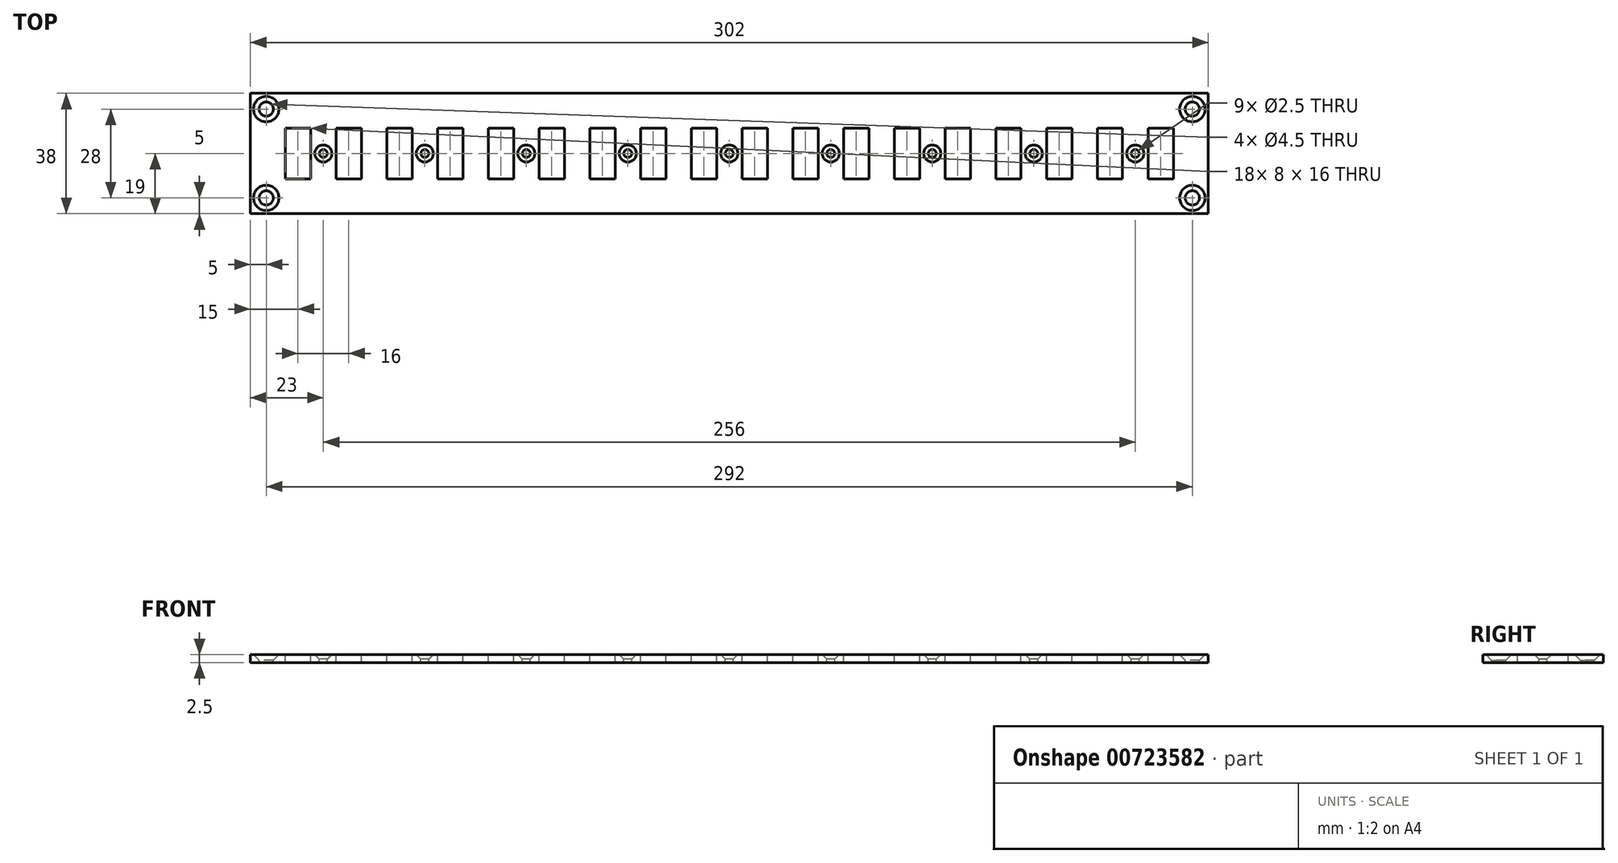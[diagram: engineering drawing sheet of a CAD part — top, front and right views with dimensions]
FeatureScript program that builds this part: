
annotation { "Feature Type Name" : "Feature", "Feature Type Description" : "" }
export const myFeature = defineFeature(function(context is Context, id is Id, definition is map)
    precondition{}
    {
        {
            var Q0;
            Q0=qCreatedBy(makeId("Top.planeOp"),FACE);
            var sketch = newSketch(context, id + "F0", { "sketchPlane" : qUnion([Q0])});
            skLineSegment(sketch, "E0.bottom", {"start": v(151, 19) * mm, "end": v(-151, 19) * mm});
            skLineSegment(sketch, "E0.top", {"start": v(151, -19) * mm, "end": v(-151, -19) * mm});
            skLineSegment(sketch, "E0.left", {"start": v(151, 19) * mm, "end": v(151, -19) * mm});
            skLineSegment(sketch, "E0.right", {"start": v(-151, 19) * mm, "end": v(-151, -19) * mm});
            skPoint(sketch, "E0.middle", {"position": v(0, 0) * mm});
            skLineSegment(sketch, "E1", {"start": v(-151, 0) * mm, "end": v(151, 0) * mm, "construction": true});
            skPoint(sketch, "E2", {"position": v(128, 0) * mm});
            skPoint(sketch, "E3", {"position": v(96, 0) * mm});
            skPoint(sketch, "E4", {"position": v(64, 0) * mm});
            skPoint(sketch, "E5", {"position": v(32, 0) * mm});
            skLineSegment(sketch, "E6", {"start": v(0, -19) * mm, "end": v(0, 19) * mm, "construction": true});
            skPoint(sketch, "E7.MirrorP", {"position": v(-32, 0) * mm});
            skPoint(sketch, "E8.MirrorP", {"position": v(-64, 0) * mm});
            skPoint(sketch, "E9.MirrorP", {"position": v(-96, 0) * mm});
            skPoint(sketch, "E10.MirrorP", {"position": v(-128, 0) * mm});
            skPoint(sketch, "E11", {"position": v(146, -14) * mm});
            skPoint(sketch, "E12.MirrorP", {"position": v(-146, -14) * mm});
            skPoint(sketch, "E13.MirrorP", {"position": v(146, 14) * mm});
            skPoint(sketch, "E14.MirrorP", {"position": v(-146, 14) * mm});
            skLineSegment(sketch, "E15", {"start": v(-151, 37.85) * mm, "end": v(-136, 37.85) * mm, "construction": true});
            skLineSegment(sketch, "E16", {"start": v(-136, 37.85) * mm, "end": v(-136, -40.42) * mm, "construction": true});
            skLineSegment(sketch, "E17.bottom", {"start": v(-132, 8) * mm, "end": v(-140, 8) * mm});
            skLineSegment(sketch, "E17.top", {"start": v(-132, -8) * mm, "end": v(-140, -8) * mm});
            skLineSegment(sketch, "E17.left", {"start": v(-132, 8) * mm, "end": v(-132, -8) * mm});
            skLineSegment(sketch, "E17.right", {"start": v(-140, 8) * mm, "end": v(-140, -8) * mm});
            skPoint(sketch, "E17.middle", {"position": v(-136, 0) * mm});
            skLineSegment(sketch, "E18.1.0.0", {"start": v(-116, 8) * mm, "end": v(-124, 8) * mm});
            skLineSegment(sketch, "E18.1.0.1", {"start": v(-116, 8) * mm, "end": v(-116, -8) * mm});
            skLineSegment(sketch, "E18.1.0.2", {"start": v(-124, 8) * mm, "end": v(-124, -8) * mm});
            skLineSegment(sketch, "E18.1.0.3", {"start": v(-116, -8) * mm, "end": v(-124, -8) * mm});
            skLineSegment(sketch, "E18.2.0.0", {"start": v(-100, 8) * mm, "end": v(-108, 8) * mm});
            skLineSegment(sketch, "E18.2.0.1", {"start": v(-100, 8) * mm, "end": v(-100, -8) * mm});
            skLineSegment(sketch, "E18.2.0.2", {"start": v(-108, 8) * mm, "end": v(-108, -8) * mm});
            skLineSegment(sketch, "E18.2.0.3", {"start": v(-100, -8) * mm, "end": v(-108, -8) * mm});
            skLineSegment(sketch, "E18.3.0.0", {"start": v(-84, 8) * mm, "end": v(-92, 8) * mm});
            skLineSegment(sketch, "E18.3.0.1", {"start": v(-84, 8) * mm, "end": v(-84, -8) * mm});
            skLineSegment(sketch, "E18.3.0.2", {"start": v(-92, 8) * mm, "end": v(-92, -8) * mm});
            skLineSegment(sketch, "E18.3.0.3", {"start": v(-84, -8) * mm, "end": v(-92, -8) * mm});
            skLineSegment(sketch, "E18.4.0.0", {"start": v(-68, 8) * mm, "end": v(-76, 8) * mm});
            skLineSegment(sketch, "E18.4.0.1", {"start": v(-68, 8) * mm, "end": v(-68, -8) * mm});
            skLineSegment(sketch, "E18.4.0.2", {"start": v(-76, 8) * mm, "end": v(-76, -8) * mm});
            skLineSegment(sketch, "E18.4.0.3", {"start": v(-68, -8) * mm, "end": v(-76, -8) * mm});
            skLineSegment(sketch, "E18.5.0.0", {"start": v(-52, 8) * mm, "end": v(-60, 8) * mm});
            skLineSegment(sketch, "E18.5.0.1", {"start": v(-52, 8) * mm, "end": v(-52, -8) * mm});
            skLineSegment(sketch, "E18.5.0.2", {"start": v(-60, 8) * mm, "end": v(-60, -8) * mm});
            skLineSegment(sketch, "E18.5.0.3", {"start": v(-52, -8) * mm, "end": v(-60, -8) * mm});
            skLineSegment(sketch, "E18.6.0.0", {"start": v(-36, 8) * mm, "end": v(-44, 8) * mm});
            skLineSegment(sketch, "E18.6.0.1", {"start": v(-36, 8) * mm, "end": v(-36, -8) * mm});
            skLineSegment(sketch, "E18.6.0.2", {"start": v(-44, 8) * mm, "end": v(-44, -8) * mm});
            skLineSegment(sketch, "E18.6.0.3", {"start": v(-36, -8) * mm, "end": v(-44, -8) * mm});
            skLineSegment(sketch, "E18.7.0.0", {"start": v(-20, 8) * mm, "end": v(-28, 8) * mm});
            skLineSegment(sketch, "E18.7.0.1", {"start": v(-20, 8) * mm, "end": v(-20, -8) * mm});
            skLineSegment(sketch, "E18.7.0.2", {"start": v(-28, 8) * mm, "end": v(-28, -8) * mm});
            skLineSegment(sketch, "E18.7.0.3", {"start": v(-20, -8) * mm, "end": v(-28, -8) * mm});
            skLineSegment(sketch, "E18.8.0.0", {"start": v(-4, 8) * mm, "end": v(-12, 8) * mm});
            skLineSegment(sketch, "E18.8.0.1", {"start": v(-4, 8) * mm, "end": v(-4, -8) * mm});
            skLineSegment(sketch, "E18.8.0.2", {"start": v(-12, 8) * mm, "end": v(-12, -8) * mm});
            skLineSegment(sketch, "E18.8.0.3", {"start": v(-4, -8) * mm, "end": v(-12, -8) * mm});
            skLineSegment(sketch, "E18.9.0.0", {"start": v(12, 8) * mm, "end": v(4, 8) * mm});
            skLineSegment(sketch, "E18.9.0.1", {"start": v(12, 8) * mm, "end": v(12, -8) * mm});
            skLineSegment(sketch, "E18.9.0.2", {"start": v(4, 8) * mm, "end": v(4, -8) * mm});
            skLineSegment(sketch, "E18.9.0.3", {"start": v(12, -8) * mm, "end": v(4, -8) * mm});
            skLineSegment(sketch, "E18.10.0.0", {"start": v(28, 8) * mm, "end": v(20, 8) * mm});
            skLineSegment(sketch, "E18.10.0.1", {"start": v(28, 8) * mm, "end": v(28, -8) * mm});
            skLineSegment(sketch, "E18.10.0.2", {"start": v(20, 8) * mm, "end": v(20, -8) * mm});
            skLineSegment(sketch, "E18.10.0.3", {"start": v(28, -8) * mm, "end": v(20, -8) * mm});
            skLineSegment(sketch, "E18.11.0.0", {"start": v(44, 8) * mm, "end": v(36, 8) * mm});
            skLineSegment(sketch, "E18.11.0.1", {"start": v(44, 8) * mm, "end": v(44, -8) * mm});
            skLineSegment(sketch, "E18.11.0.2", {"start": v(36, 8) * mm, "end": v(36, -8) * mm});
            skLineSegment(sketch, "E18.11.0.3", {"start": v(44, -8) * mm, "end": v(36, -8) * mm});
            skLineSegment(sketch, "E18.12.0.0", {"start": v(60, 8) * mm, "end": v(52, 8) * mm});
            skLineSegment(sketch, "E18.12.0.1", {"start": v(60, 8) * mm, "end": v(60, -8) * mm});
            skLineSegment(sketch, "E18.12.0.2", {"start": v(52, 8) * mm, "end": v(52, -8) * mm});
            skLineSegment(sketch, "E18.12.0.3", {"start": v(60, -8) * mm, "end": v(52, -8) * mm});
            skLineSegment(sketch, "E18.13.0.0", {"start": v(76, 8) * mm, "end": v(68, 8) * mm});
            skLineSegment(sketch, "E18.13.0.1", {"start": v(76, 8) * mm, "end": v(76, -8) * mm});
            skLineSegment(sketch, "E18.13.0.2", {"start": v(68, 8) * mm, "end": v(68, -8) * mm});
            skLineSegment(sketch, "E18.13.0.3", {"start": v(76, -8) * mm, "end": v(68, -8) * mm});
            skLineSegment(sketch, "E18.14.0.0", {"start": v(92, 8) * mm, "end": v(84, 8) * mm});
            skLineSegment(sketch, "E18.14.0.1", {"start": v(92, 8) * mm, "end": v(92, -8) * mm});
            skLineSegment(sketch, "E18.14.0.2", {"start": v(84, 8) * mm, "end": v(84, -8) * mm});
            skLineSegment(sketch, "E18.14.0.3", {"start": v(92, -8) * mm, "end": v(84, -8) * mm});
            skLineSegment(sketch, "E18.15.0.0", {"start": v(108, 8) * mm, "end": v(100, 8) * mm});
            skLineSegment(sketch, "E18.15.0.1", {"start": v(108, 8) * mm, "end": v(108, -8) * mm});
            skLineSegment(sketch, "E18.15.0.2", {"start": v(100, 8) * mm, "end": v(100, -8) * mm});
            skLineSegment(sketch, "E18.15.0.3", {"start": v(108, -8) * mm, "end": v(100, -8) * mm});
            skLineSegment(sketch, "E18.16.0.0", {"start": v(124, 8) * mm, "end": v(116, 8) * mm});
            skLineSegment(sketch, "E18.16.0.1", {"start": v(124, 8) * mm, "end": v(124, -8) * mm});
            skLineSegment(sketch, "E18.16.0.2", {"start": v(116, 8) * mm, "end": v(116, -8) * mm});
            skLineSegment(sketch, "E18.16.0.3", {"start": v(124, -8) * mm, "end": v(116, -8) * mm});
            skLineSegment(sketch, "E18.17.0.0", {"start": v(140, 8) * mm, "end": v(132, 8) * mm});
            skLineSegment(sketch, "E18.17.0.1", {"start": v(140, 8) * mm, "end": v(140, -8) * mm});
            skLineSegment(sketch, "E18.17.0.2", {"start": v(132, 8) * mm, "end": v(132, -8) * mm});
            skLineSegment(sketch, "E18.17.0.3", {"start": v(140, -8) * mm, "end": v(132, -8) * mm});
            skLineSegment(sketch, "E18.direction1", {"start": v(-140, -8) * mm, "end": v(-124, -8) * mm, "construction": true});
            skSolve(sketch);
        }
        {
            var Q0;
            Q0=makeQuery(id+"F0.imprint","IMPRINT",FACE,{"disambiguationData":[TD([[makeQuery(id+"F0.imprint","IMPRINT",EDGE,{"derivedFrom":sQuery(id+"F0.wireOp",EDGE,"E0.bottom")}),1.0]])]});
            extrude(context, id + "F1", {"entities" : qUnion([Q0]), "oppositeDirection" : true, "depth" : 2.5 * mm, "offsetDistance" : 25 * mm});
        }
        {
            var Q0;
            Q0=sQuery(id+"F0.wireOp",VERTEX,"E10.MirrorP");
            var Q1;
            Q1=sQuery(id+"F0.wireOp",VERTEX,"E9.MirrorP");
            var Q2;
            Q2=sQuery(id+"F0.wireOp",VERTEX,"E8.MirrorP");
            var Q3;
            Q3=sQuery(id+"F0.wireOp",VERTEX,"E7.MirrorP");
            var Q4;
            Q4=sQuery(id+"F0.wireOp",VERTEX,"E0.middle");
            var Q5;
            Q5=sQuery(id+"F0.wireOp",VERTEX,"E5");
            var Q6;
            Q6=sQuery(id+"F0.wireOp",VERTEX,"E4");
            var Q7;
            Q7=sQuery(id+"F0.wireOp",VERTEX,"E3");
            var Q8;
            Q8=sQuery(id+"F0.wireOp",VERTEX,"E2");
            var Q9;
            Q9=makeQuery(id+"F1.opExtrude","SWEPT_BODY",BODY,{"disambiguationData":[OSD([sQuery(id+"F0.wireOp",EDGE,"E0.bottom"),sQuery(id+"F0.wireOp",EDGE,"E0.top"),sQuery(id+"F0.wireOp",EDGE,"E0.left"),sQuery(id+"F0.wireOp",EDGE,"E0.right")])]});
            hole(context, id + "F2", {"style" : HoleStyle.C_SINK, "endStyle" : HoleEndStyle.THROUGH, "holeDiameter" : 2.5 * mm, "cSinkDiameter" : 5.4 * mm, "cSinkAngle" : 90 * degree, "majorDiameter" : 5 * mm, "isTappedThrough" : true, "tappedDepth" : 12 * mm, "tapClearance" : 3, "startFromSketch" : true, "locations" : qUnion([Q0, Q1, Q2, Q3, Q4, Q5, Q6, Q7, Q8]), "scope" : qUnion([Q9])});
        }
        {
            var Q0;
            Q0=sQuery(id+"F0.wireOp",VERTEX,"E14.MirrorP");
            var Q1;
            Q1=sQuery(id+"F0.wireOp",VERTEX,"E12.MirrorP");
            var Q2;
            Q2=sQuery(id+"F0.wireOp",VERTEX,"E13.MirrorP");
            var Q3;
            Q3=sQuery(id+"F0.wireOp",VERTEX,"E11");
            var Q4;
            Q4=makeQuery(id+"F1.opExtrude","SWEPT_BODY",BODY,{"disambiguationData":[OSD([sQuery(id+"F0.wireOp",EDGE,"E0.bottom"),sQuery(id+"F0.wireOp",EDGE,"E0.top"),sQuery(id+"F0.wireOp",EDGE,"E0.left"),sQuery(id+"F0.wireOp",EDGE,"E0.right")])]});
            hole(context, id + "F3", {"style" : HoleStyle.C_SINK, "endStyle" : HoleEndStyle.THROUGH, "holeDiameter" : 4.5 * mm, "cSinkDiameter" : 8 * mm, "cSinkAngle" : 90 * degree, "majorDiameter" : 5 * mm, "isTappedThrough" : true, "tappedDepth" : 12 * mm, "tapClearance" : 3, "startFromSketch" : true, "locations" : qUnion([Q0, Q1, Q2, Q3]), "scope" : qUnion([Q4])});
        }
        {
            var Q0;
            Q0=makeQuery(id+"F0.imprint","IMPRINT",FACE,{"disambiguationData":[TD([[makeQuery(id+"F0.imprint","IMPRINT",EDGE,{"derivedFrom":sQuery(id+"F0.wireOp",EDGE,"E17.bottom")}),1.0]])]});
            extrude(context, id + "F4", {"entities" : qUnion([Q0]), "operationType" : NewBodyOperationType.REMOVE, "endBound" : BoundingType.THROUGH_ALL, "oppositeDirection" : true, "depth" : 25 * mm, "offsetDistance" : 25 * mm});
        }
    });
